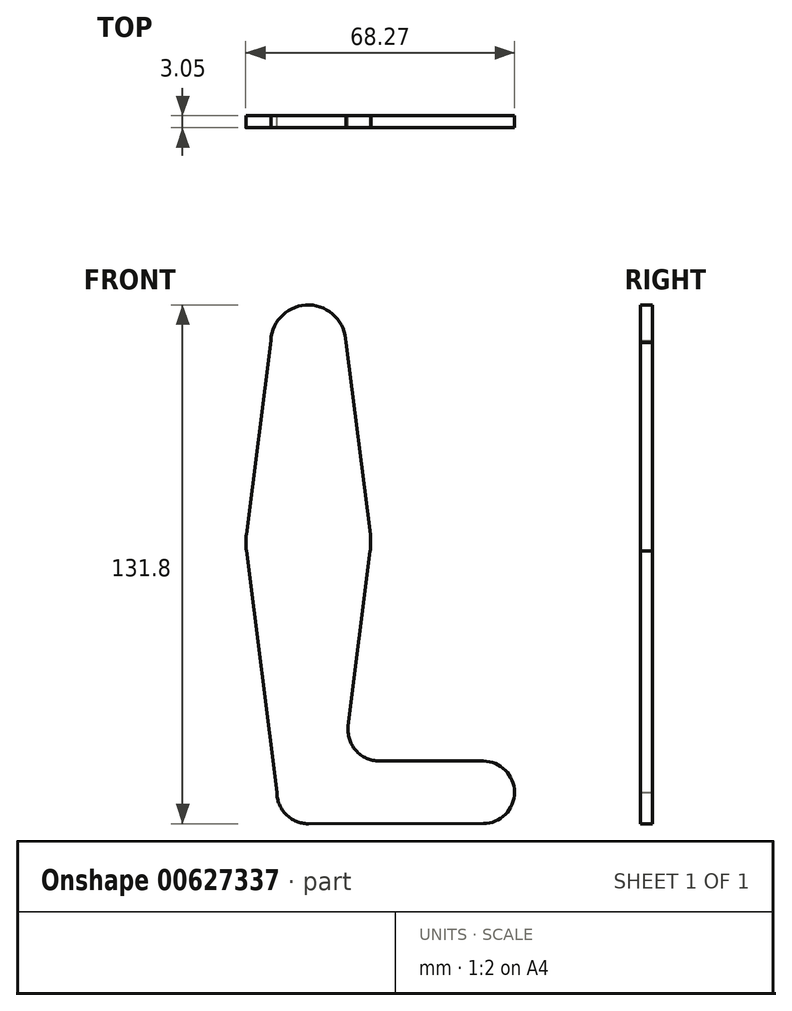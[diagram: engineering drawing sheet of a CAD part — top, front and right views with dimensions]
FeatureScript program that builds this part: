
annotation { "Feature Type Name" : "Feature", "Feature Type Description" : "" }
export const myFeature = defineFeature(function(context is Context, id is Id, definition is map)
    precondition{}
    {
        {
            var Q0;
            Q0=qCreatedBy(makeId("Front.planeOp"),FACE);
            var sketch = newSketch(context, id + "F0", { "sketchPlane" : qUnion([Q0])});
            skLineSegment(sketch, "E0", {"start": v(0, 0) * mm, "end": v(0, 63.5) * mm});
            skCircle(sketch, "E1", {"center": v(0, 63.5) * mm, "radius": 15.88 * mm});
            skLineSegment(sketch, "E2", {"start": v(0, 63.5) * mm, "end": v(0, 114.3) * mm});
            skCircle(sketch, "E3", {"center": v(0, 114.3) * mm, "radius": 9.52 * mm});
            skLineSegment(sketch, "E4", {"start": v(0, 0) * mm, "end": v(44.45, 0) * mm});
            skCircle(sketch, "E5", {"center": v(0, 0) * mm, "radius": 7.97 * mm});
            skCircle(sketch, "E6", {"center": v(44.45, 0) * mm, "radius": 7.94 * mm});
            skLineSegment(sketch, "E7", {"start": v(-7.97, 0) * mm, "end": v(-15.75, 61.5) * mm});
            skLineSegment(sketch, "E8", {"start": v(-15.75, 65.5) * mm, "end": v(-9.51, 114.82) * mm});
            skLineSegment(sketch, "E9", {"start": v(9.53, 114.3) * mm, "end": v(15.75, 65.5) * mm});
            skLineSegment(sketch, "E10", {"start": v(15.75, 61.5) * mm, "end": v(10.15, 16.9) * mm});
            skLineSegment(sketch, "E11", {"start": v(0, -7.97) * mm, "end": v(44.46, -7.94) * mm});
            skLineSegment(sketch, "E12", {"start": v(18.03, 7.96) * mm, "end": v(44.46, 7.94) * mm});
            skPoint(sketch, "E13.newPointA", {"position": v(8.03, 0) * mm});
            skPoint(sketch, "E13.newPointB", {"position": v(0, 7.97) * mm});
            skArc(sketch, "E13.filletArc", {"start": v(10.15, 16.9) * mm, "mid": v(12.08, 10.65) * mm, "end": v(18.03, 7.96) * mm});
            skSolve(sketch);
        }
        {
            var Q0;
            Q0=qCreatedBy(makeId("Front.planeOp"),FACE);
            var sketch = newSketch(context, id + "F1", { "sketchPlane" : qUnion([Q0])});
            skCircle(sketch, "E14", {"center": v(0, 0) * mm, "radius": 3.18 * mm});
            skCircle(sketch, "E15", {"center": v(0, 114.3) * mm, "radius": 3.18 * mm});
            skCircle(sketch, "E16", {"center": v(44.45, 0) * mm, "radius": 3.17 * mm});
            skCircle(sketch, "E17", {"center": v(0, 167.43) * mm, "radius": 38.1 * mm});
            skCircle(sketch, "E18", {"center": v(-3.18, 100.03) * mm, "radius": 3.18 * mm});
            skSolve(sketch);
        }
        {
            var Q0;
            {var subQ3=sQuery(id+"F0.wireOp",EDGE,"E0");var subQ5=sQuery(id+"F0.wireOp",EDGE,"E4");var subQ6=makeQuery(id+"F0.imprint","INTERSECT",VERTEX,{"derivedFrom":[subQ3,subQ5]});Q0=makeQuery(id+"F0.imprint","IMPRINT",FACE,{"disambiguationData":[TD([[makeQuery(id+"F0.imprint","IMPRINT",EDGE,{"disambiguationData":[TD([[subQ6,-1.0]])],"derivedFrom":subQ3}),1.0]])]});}
            var Q1;
            {var subQ5=sQuery(id+"F0.wireOp",EDGE,"E7");Q1=makeQuery(id+"F0.imprint","IMPRINT",FACE,{"disambiguationData":[TD([[makeQuery(id+"F0.imprint","IMPRINT",EDGE,{"derivedFrom":subQ5}),-1.0]])]});}
            var Q2;
            {var subQ3=sQuery(id+"F0.wireOp",EDGE,"E2");var subQ5=sQuery(id+"F0.wireOp",EDGE,"E0");var subQ7=makeQuery(id+"F0.imprint","INTERSECT",VERTEX,{"derivedFrom":[subQ5,subQ3]});Q2=makeQuery(id+"F0.imprint","IMPRINT",FACE,{"disambiguationData":[TD([[makeQuery(id+"F0.imprint","IMPRINT",EDGE,{"disambiguationData":[TD([[subQ7,1.0]])],"derivedFrom":subQ5}),-1.0]])]});}
            var Q3;
            {var subQ2=sQuery(id+"F0.wireOp",EDGE,"E0");var subQ5=sQuery(id+"F0.wireOp",EDGE,"E2");var subQ7=makeQuery(id+"F0.imprint","INTERSECT",VERTEX,{"derivedFrom":[subQ2,subQ5]});Q3=makeQuery(id+"F0.imprint","IMPRINT",FACE,{"disambiguationData":[TD([[makeQuery(id+"F0.imprint","IMPRINT",EDGE,{"disambiguationData":[TD([[subQ7,1.0]])],"derivedFrom":subQ2}),1.0]])]});}
            var Q4;
            {var subQ5=sQuery(id+"F0.wireOp",EDGE,"E11");Q4=makeQuery(id+"F0.imprint","IMPRINT",FACE,{"disambiguationData":[TD([[makeQuery(id+"F0.imprint","IMPRINT",EDGE,{"derivedFrom":subQ5}),1.0]])]});}
            var Q5;
            {var subQ12=sQuery(id+"F0.wireOp",EDGE,"E12");Q5=makeQuery(id+"F0.imprint","IMPRINT",FACE,{"disambiguationData":[TD([[makeQuery(id+"F0.imprint","IMPRINT",EDGE,{"derivedFrom":subQ12}),-1.0]])]});}
            var Q6;
            {var subQ0=sQuery(id+"F0.wireOp",EDGE,"E9");Q6=makeQuery(id+"F0.imprint","IMPRINT",FACE,{"disambiguationData":[TD([[makeQuery(id+"F0.imprint","IMPRINT",EDGE,{"derivedFrom":subQ0}),-1.0]])]});}
            var Q7;
            {var subQ0=sQuery(id+"F0.wireOp",EDGE,"E8");Q7=makeQuery(id+"F0.imprint","IMPRINT",FACE,{"disambiguationData":[TD([[makeQuery(id+"F0.imprint","IMPRINT",EDGE,{"derivedFrom":subQ0}),-1.0]])]});}
            var Q8;
            {var subQ0=sQuery(id+"F0.wireOp",EDGE,"E4");var subQ1=sQuery(id+"F0.wireOp",EDGE,"E0");var subQ2=makeQuery(id+"F0.imprint","INTERSECT",VERTEX,{"derivedFrom":[subQ1,subQ0]});Q8=makeQuery(id+"F0.imprint","IMPRINT",FACE,{"disambiguationData":[TD([[makeQuery(id+"F0.imprint","IMPRINT",EDGE,{"disambiguationData":[TD([[subQ2,-1.0]])],"derivedFrom":subQ1}),-1.0]])]});}
            var Q9;
            {var subQ0=sQuery(id+"F0.wireOp",EDGE,"E6");var subQ1=makeQuery(id+"F0.imprint","INTERSECT",VERTEX,{"derivedFrom":[subQ0,sQuery(id+"F0.wireOp",EDGE,"E12")]});Q9=makeQuery(id+"F0.imprint","IMPRINT",FACE,{"disambiguationData":[TD([[makeQuery(id+"F0.imprint","IMPRINT",EDGE,{"disambiguationData":[TD([[subQ1,-1.0]])],"derivedFrom":subQ0}),1.0]])]});}
            var Q10;
            {var subQ0=sQuery(id+"F0.wireOp",EDGE,"E3");var subQ1=makeQuery(id+"F0.imprint","INTERSECT",VERTEX,{"derivedFrom":[subQ0,sQuery(id+"F0.wireOp",EDGE,"E8")]});Q10=makeQuery(id+"F0.imprint","IMPRINT",FACE,{"disambiguationData":[TD([[makeQuery(id+"F0.imprint","IMPRINT",EDGE,{"disambiguationData":[TD([[subQ1,1.0]])],"derivedFrom":subQ0}),1.0]])]});}
            extrude(context, id + "F2", {"entities" : qUnion([Q0, Q1, Q2, Q3, Q4, Q5, Q6, Q7, Q8, Q9, Q10]), "depth" : 3.05 * mm, "offsetDistance" : 25.4 * mm});
        }
        {
            var Q0;
            Q0 = qSketchRegion(id + "F1", true);
            extrude(context, id + "F3", {"entities" : qUnion([Q0]), "operationType" : NewBodyOperationType.REMOVE, "oppositeDirection" : true, "depth" : 25.4 * mm, "offsetDistance" : 25.4 * mm});
        }
    });
